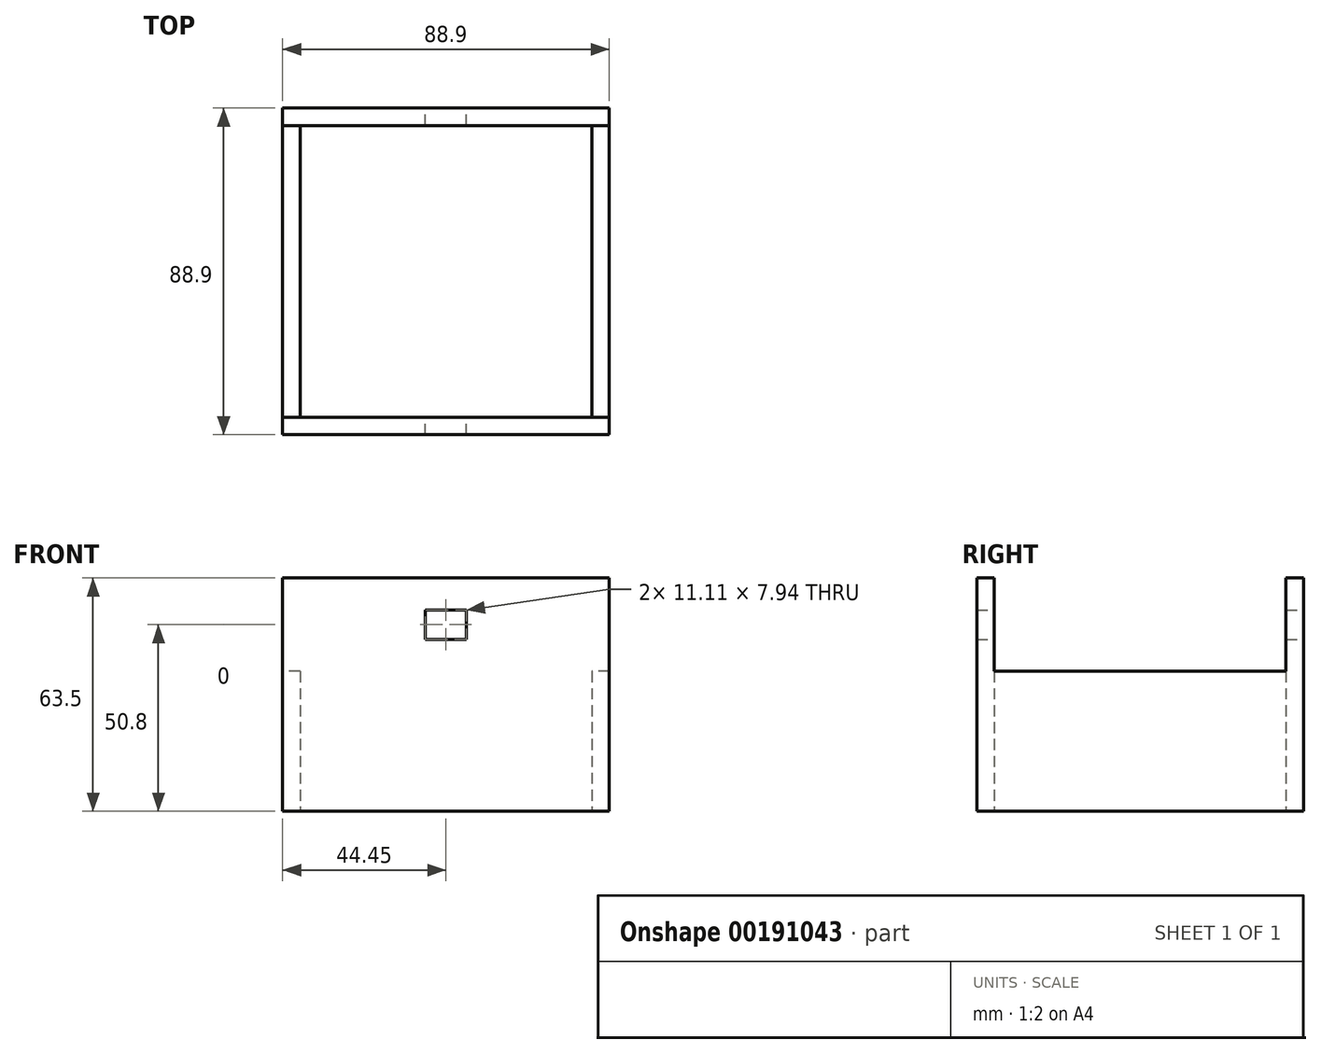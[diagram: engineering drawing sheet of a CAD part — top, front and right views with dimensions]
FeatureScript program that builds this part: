
annotation { "Feature Type Name" : "Feature", "Feature Type Description" : "" }
export const myFeature = defineFeature(function(context is Context, id is Id, definition is map)
    precondition{}
    {
        {
            var Q0;
            Q0=qCreatedBy(makeId("Top.planeOp"),FACE);
            var sketch = newSketch(context, id + "F0", { "sketchPlane" : qUnion([Q0])});
            skLineSegment(sketch, "E0.bottom", {"start": v(44.45, 44.45) * mm, "end": v(-44.45, 44.45) * mm});
            skLineSegment(sketch, "E0.top", {"start": v(44.45, -44.45) * mm, "end": v(-44.45, -44.45) * mm});
            skLineSegment(sketch, "E0.left", {"start": v(44.45, 44.45) * mm, "end": v(44.45, -44.45) * mm});
            skLineSegment(sketch, "E0.right", {"start": v(-44.45, 44.45) * mm, "end": v(-44.45, -44.45) * mm});
            skPoint(sketch, "E0.middle", {"position": v(0, 0) * mm});
            skLineSegment(sketch, "E1.bottom", {"start": v(39.69, 39.69) * mm, "end": v(-39.69, 39.69) * mm});
            skLineSegment(sketch, "E1.top", {"start": v(39.69, -39.69) * mm, "end": v(-39.69, -39.69) * mm});
            skLineSegment(sketch, "E1.left", {"start": v(39.69, 39.69) * mm, "end": v(39.69, -39.69) * mm});
            skLineSegment(sketch, "E1.right", {"start": v(-39.69, 39.69) * mm, "end": v(-39.69, -39.69) * mm});
            skSolve(sketch);
        }
        {
            var Q0;
            Q0=makeQuery(id+"F0.imprint","IMPRINT",FACE,{"disambiguationData":[TD([[makeQuery(id+"F0.imprint","IMPRINT",EDGE,{"derivedFrom":sQuery(id+"F0.wireOp",EDGE,"E0.bottom")}),1.0]])]});
            extrude(context, id + "F1", {"entities" : qUnion([Q0]), "depth" : 63.5 * mm});
        }
        {
            var Q0;
            Q0=makeQuery(id+"F1.opExtrude","SWEPT_FACE",FACE,{"disambiguationData":[OSD([sQuery(id+"F0.wireOp",EDGE,"E0.right")])]});
            var sketch = newSketch(context, id + "F2", { "sketchPlane" : qUnion([Q0])});
            skLineSegment(sketch, "E2", {"start": v(44.45, 63.5) * mm, "end": v(44.45, 38.1) * mm});
            skPoint(sketch, "E3", {"position": v(44.45, 50.8) * mm});
            skPoint(sketch, "E4", {"position": v(0, 50.8) * mm});
            skLineSegment(sketch, "E5", {"start": v(44.45, 38.1) * mm, "end": v(39.69, 38.1) * mm});
            skPoint(sketch, "E6", {"position": v(-39.69, 38.1) * mm});
            skPoint(sketch, "E7.trimOffspring.end.orphan", {"position": v(-44.45, 50.8) * mm});
            skPoint(sketch, "E8.end.orphan", {"position": v(-44.45, 38.1) * mm});
            skLineSegment(sketch, "E9.bottom", {"start": v(39.69, 38.1) * mm, "end": v(-39.69, 38.1) * mm});
            skLineSegment(sketch, "E9.top", {"start": v(39.69, 63.5) * mm, "end": v(-39.69, 63.5) * mm});
            skLineSegment(sketch, "E9.left", {"start": v(39.69, 38.1) * mm, "end": v(39.69, 63.5) * mm});
            skLineSegment(sketch, "E9.right", {"start": v(-39.69, 38.1) * mm, "end": v(-39.69, 63.5) * mm});
            skSolve(sketch);
        }
        {
            var Q0;
            Q0=makeQuery(id+"F1.opExtrude","SWEPT_FACE",FACE,{"disambiguationData":[OSD([sQuery(id+"F0.wireOp",EDGE,"E0.bottom")])]});
            var sketch = newSketch(context, id + "F3", { "sketchPlane" : qUnion([Q0])});
            skLineSegment(sketch, "E10", {"start": v(0, 63.5) * mm, "end": v(0, 38.1) * mm});
            skPoint(sketch, "E10.endSnap0", {"position": v(0, 63.5) * mm});
            skPoint(sketch, "E11", {"position": v(0, 50.8) * mm});
            skLineSegment(sketch, "E12.bottom", {"start": v(5.56, 54.77) * mm, "end": v(-5.56, 54.77) * mm});
            skLineSegment(sketch, "E12.top", {"start": v(5.56, 46.83) * mm, "end": v(-5.56, 46.83) * mm});
            skLineSegment(sketch, "E12.left", {"start": v(5.56, 54.77) * mm, "end": v(5.56, 46.83) * mm});
            skLineSegment(sketch, "E12.right", {"start": v(-5.56, 54.77) * mm, "end": v(-5.56, 46.83) * mm});
            skSolve(sketch);
        }
        {
            var Q0;
            Q0 = qSketchRegion(id + "F3", true);
            extrude(context, id + "F4", {"entities" : qUnion([Q0]), "operationType" : NewBodyOperationType.REMOVE, "endBound" : BoundingType.THROUGH_ALL, "oppositeDirection" : true, "depth" : 25.4 * mm});
        }
        {
            var Q0;
            Q0 = qSketchRegion(id + "F2", true);
            extrude(context, id + "F5", {"entities" : qUnion([Q0]), "operationType" : NewBodyOperationType.REMOVE, "endBound" : BoundingType.THROUGH_ALL, "oppositeDirection" : true, "depth" : 25.4 * mm});
        }
    });
